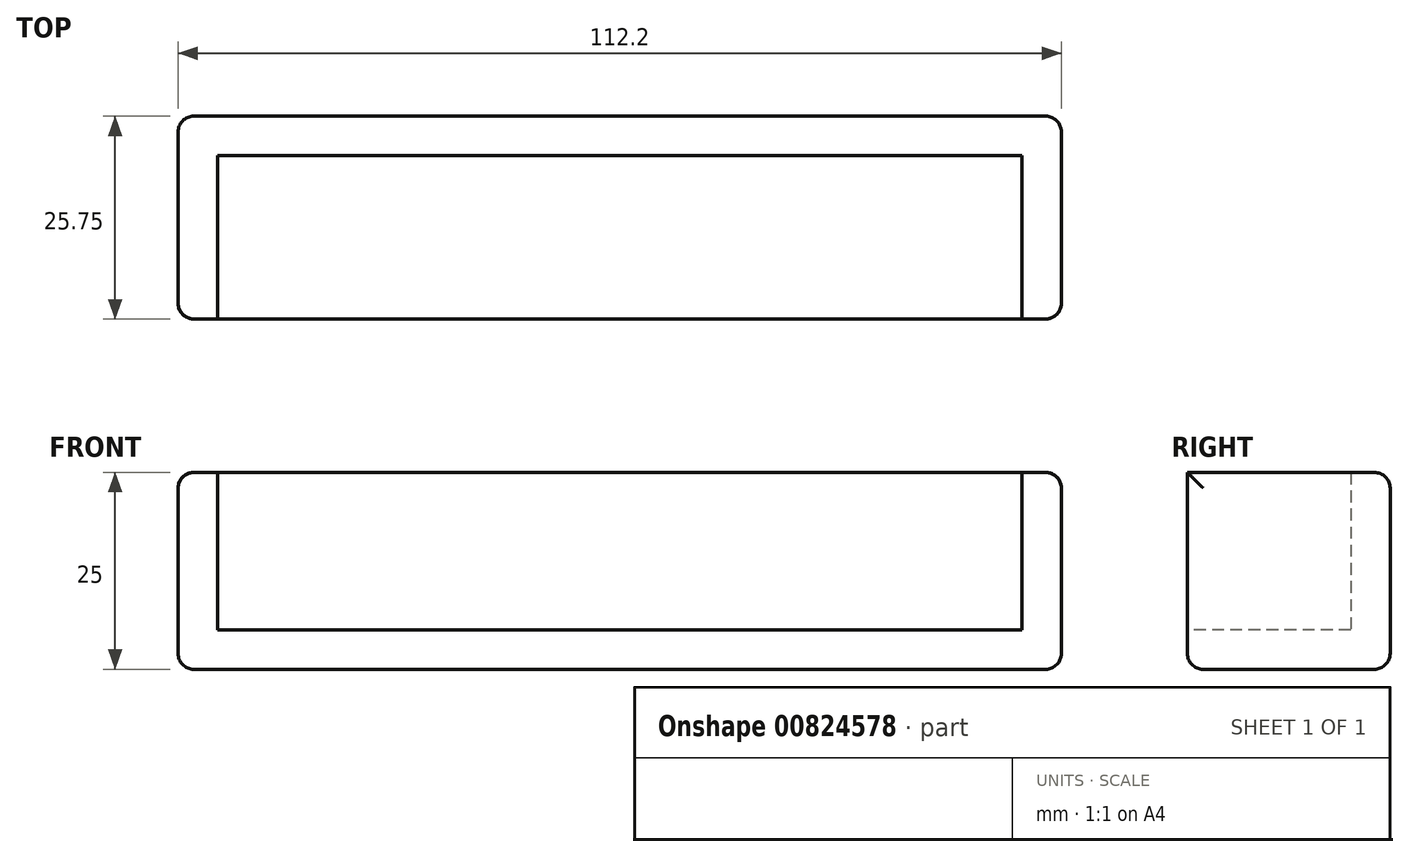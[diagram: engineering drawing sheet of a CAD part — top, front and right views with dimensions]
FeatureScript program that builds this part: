
annotation { "Feature Type Name" : "Feature", "Feature Type Description" : "" }
export const myFeature = defineFeature(function(context is Context, id is Id, definition is map)
    precondition{}
    {
        {
            var Q0;
            Q0=qCreatedBy(makeId("Top.planeOp"),FACE);
            var sketch = newSketch(context, id + "F0", { "sketchPlane" : qUnion([Q0])});
            skLineSegment(sketch, "E0.bottom", {"start": v(-26.8, 28.97) * mm, "end": v(75.4, 28.97) * mm});
            skLineSegment(sketch, "E0.top", {"start": v(-26.8, 8.22) * mm, "end": v(75.4, 8.22) * mm});
            skLineSegment(sketch, "E0.left", {"start": v(-26.8, 28.97) * mm, "end": v(-26.8, 8.22) * mm});
            skLineSegment(sketch, "E0.right", {"start": v(75.4, 28.97) * mm, "end": v(75.4, 8.22) * mm});
            skSolve(sketch);
        }
        {
            var Q0;
            Q0=qSketchRegion(id+"F0",true);
            extrude(context, id + "F1", {"entities" : qUnion([Q0]), "depth" : 5 * mm, "offsetDistance" : 25 * mm});
        }
        {
            var Q0;
            Q0=makeQuery(id+"F1.opExtrude","SWEPT_FACE",FACE,{"disambiguationData":[OSD([sQuery(id+"F0.wireOp",EDGE,"E0.right")])]});
            var sketch = newSketch(context, id + "F2", { "sketchPlane" : qUnion([Q0])});
            skLineSegment(sketch, "E1.bottom", {"start": v(8.22, 0) * mm, "end": v(28.97, 0) * mm});
            skLineSegment(sketch, "E1.top", {"start": v(8.22, 25) * mm, "end": v(28.97, 25) * mm});
            skLineSegment(sketch, "E1.left", {"start": v(8.22, 0) * mm, "end": v(8.22, 25) * mm});
            skLineSegment(sketch, "E1.right", {"start": v(28.97, 0) * mm, "end": v(28.97, 25) * mm});
            skSolve(sketch);
        }
        {
            var Q0;
            Q0=qSketchRegion(id+"F2",true);
            extrude(context, id + "F3", {"entities" : qUnion([Q0]), "operationType" : NewBodyOperationType.ADD, "depth" : 5 * mm, "offsetDistance" : 25 * mm});
        }
        {
            var Q0;
            Q0=makeQuery(id+"F1.opExtrude","SWEPT_FACE",FACE,{"disambiguationData":[OSD([sQuery(id+"F0.wireOp",EDGE,"E0.left")])]});
            var sketch = newSketch(context, id + "F4", { "sketchPlane" : qUnion([Q0])});
            skLineSegment(sketch, "E2.bottom", {"start": v(-28.97, 0) * mm, "end": v(-8.22, 0) * mm});
            skLineSegment(sketch, "E2.top", {"start": v(-28.97, 25) * mm, "end": v(-8.22, 25) * mm});
            skLineSegment(sketch, "E2.left", {"start": v(-28.97, 0) * mm, "end": v(-28.97, 25) * mm});
            skLineSegment(sketch, "E2.right", {"start": v(-8.22, 0) * mm, "end": v(-8.22, 25) * mm});
            skSolve(sketch);
        }
        {
            var Q0;
            Q0=qSketchRegion(id+"F4",true);
            extrude(context, id + "F5", {"entities" : qUnion([Q0]), "operationType" : NewBodyOperationType.ADD, "depth" : 5 * mm, "offsetDistance" : 25 * mm});
        }
        {
            var Q0;
            Q0=makeQuery(id+"F5.boolean.opBoolean","MERGE",FACE,{"derivedFrom":[makeQuery(id+"F3.boolean.opBoolean","MERGE",FACE,{"derivedFrom":[makeQuery(id+"F1.opExtrude","SWEPT_FACE",FACE,{"disambiguationData":[OSD([sQuery(id+"F0.wireOp",EDGE,"E0.bottom")])]}),makeQuery(id+"F3.opExtrude","SWEPT_FACE",FACE,{"disambiguationData":[OSD([sQuery(id+"F2.wireOp",EDGE,"E1.right")])]})]}),makeQuery(id+"F5.opExtrude","SWEPT_FACE",FACE,{"disambiguationData":[OSD([sQuery(id+"F4.wireOp",EDGE,"E2.left")])]})]});
            var sketch = newSketch(context, id + "F6", { "sketchPlane" : qUnion([Q0])});
            skLineSegment(sketch, "E3.bottom", {"start": v(-80.4, 0) * mm, "end": v(31.8, 0) * mm});
            skLineSegment(sketch, "E3.top", {"start": v(-80.4, 25) * mm, "end": v(31.8, 25) * mm});
            skLineSegment(sketch, "E3.left", {"start": v(-80.4, 0) * mm, "end": v(-80.4, 25) * mm});
            skLineSegment(sketch, "E3.right", {"start": v(31.8, 0) * mm, "end": v(31.8, 25) * mm});
            skSolve(sketch);
        }
        {
            var Q0;
            Q0=qSketchRegion(id+"F6",true);
            extrude(context, id + "F7", {"entities" : qUnion([Q0]), "operationType" : NewBodyOperationType.ADD, "depth" : 5 * mm, "offsetDistance" : 25 * mm});
        }
        {
            var Q0;
            Q0=makeQuery(id+"F7.boolean.opBoolean","MERGE",EDGE,{"derivedFrom":[makeQuery(id+"F5.opExtrude","CAP_EDGE",EDGE,{"disambiguationData":[OSD([sQuery(id+"F4.wireOp",EDGE,"E2.top")])],"isStart":false}),makeQuery(id+"F7.opExtrude","SWEPT_EDGE",EDGE,{"disambiguationData":[OSD([sQuery(id+"F6.wireOp",EDGE,"E3.top"),sQuery(id+"F6.wireOp",EDGE,"E3.right")])]})]});
            var Q1;
            Q1=makeQuery(id+"F7.boolean.opBoolean","MERGE",EDGE,{"derivedFrom":[makeQuery(id+"F3.opExtrude","CAP_EDGE",EDGE,{"disambiguationData":[OSD([sQuery(id+"F2.wireOp",EDGE,"E1.top")])],"isStart":false}),makeQuery(id+"F7.opExtrude","SWEPT_EDGE",EDGE,{"disambiguationData":[OSD([sQuery(id+"F6.wireOp",EDGE,"E3.top"),sQuery(id+"F6.wireOp",EDGE,"E3.left")])]})]});
            var Q2;
            Q2=makeQuery(id+"F7.opExtrude","CAP_EDGE",EDGE,{"disambiguationData":[OSD([sQuery(id+"F6.wireOp",EDGE,"E3.top")])],"isStart":false});
            var Q3;
            Q3=makeQuery(id+"F5.boolean.opBoolean","MERGE",EDGE,{"derivedFrom":[makeQuery(id+"F3.boolean.opBoolean","MERGE",EDGE,{"derivedFrom":[makeQuery(id+"F1.opExtrude","CAP_EDGE",EDGE,{"disambiguationData":[OSD([sQuery(id+"F0.wireOp",EDGE,"E0.top")])],"isStart":true}),makeQuery(id+"F3.opExtrude","SWEPT_EDGE",EDGE,{"disambiguationData":[OSD([sQuery(id+"F2.wireOp",EDGE,"E1.bottom"),sQuery(id+"F2.wireOp",EDGE,"E1.left")])]})]}),makeQuery(id+"F5.opExtrude","SWEPT_EDGE",EDGE,{"disambiguationData":[OSD([sQuery(id+"F4.wireOp",EDGE,"E2.bottom"),sQuery(id+"F4.wireOp",EDGE,"E2.right")])]})]});
            var Q4;
            Q4=makeQuery(id+"F7.boolean.opBoolean","MERGE",EDGE,{"derivedFrom":[makeQuery(id+"F5.opExtrude","CAP_EDGE",EDGE,{"disambiguationData":[OSD([sQuery(id+"F4.wireOp",EDGE,"E2.bottom")])],"isStart":false}),makeQuery(id+"F7.opExtrude","SWEPT_EDGE",EDGE,{"disambiguationData":[OSD([sQuery(id+"F6.wireOp",EDGE,"E3.bottom"),sQuery(id+"F6.wireOp",EDGE,"E3.right")])]})]});
            var Q5;
            Q5=makeQuery(id+"F5.opExtrude","CAP_EDGE",EDGE,{"disambiguationData":[OSD([sQuery(id+"F4.wireOp",EDGE,"E2.right")])],"isStart":false});
            var Q6;
            Q6=makeQuery(id+"F7.boolean.opBoolean","MERGE",EDGE,{"derivedFrom":[makeQuery(id+"F3.opExtrude","CAP_EDGE",EDGE,{"disambiguationData":[OSD([sQuery(id+"F2.wireOp",EDGE,"E1.bottom")])],"isStart":false}),makeQuery(id+"F7.opExtrude","SWEPT_EDGE",EDGE,{"disambiguationData":[OSD([sQuery(id+"F6.wireOp",EDGE,"E3.bottom"),sQuery(id+"F6.wireOp",EDGE,"E3.left")])]})]});
            var Q7;
            Q7=makeQuery(id+"F7.opExtrude","CAP_EDGE",EDGE,{"disambiguationData":[OSD([sQuery(id+"F6.wireOp",EDGE,"E3.bottom")])],"isStart":false});
            var Q8;
            Q8=makeQuery(id+"F7.opExtrude","CAP_EDGE",EDGE,{"disambiguationData":[OSD([sQuery(id+"F6.wireOp",EDGE,"E3.left")])],"isStart":false});
            var Q9;
            Q9=makeQuery(id+"F7.opExtrude","CAP_EDGE",EDGE,{"disambiguationData":[OSD([sQuery(id+"F6.wireOp",EDGE,"E3.right")])],"isStart":false});
            var Q10;
            Q10=makeQuery(id+"F3.opExtrude","CAP_EDGE",EDGE,{"disambiguationData":[OSD([sQuery(id+"F2.wireOp",EDGE,"E1.left")])],"isStart":false});
            fillet(context, id + "F8", {"entities" : qUnion([Q0, Q1, Q2, Q3, Q4, Q5, Q6, Q7, Q8, Q9, Q10]), "radius" : 2 * mm, "tangentPropagation" : true, "allowEdgeOverflow" : false});
        }
    });
